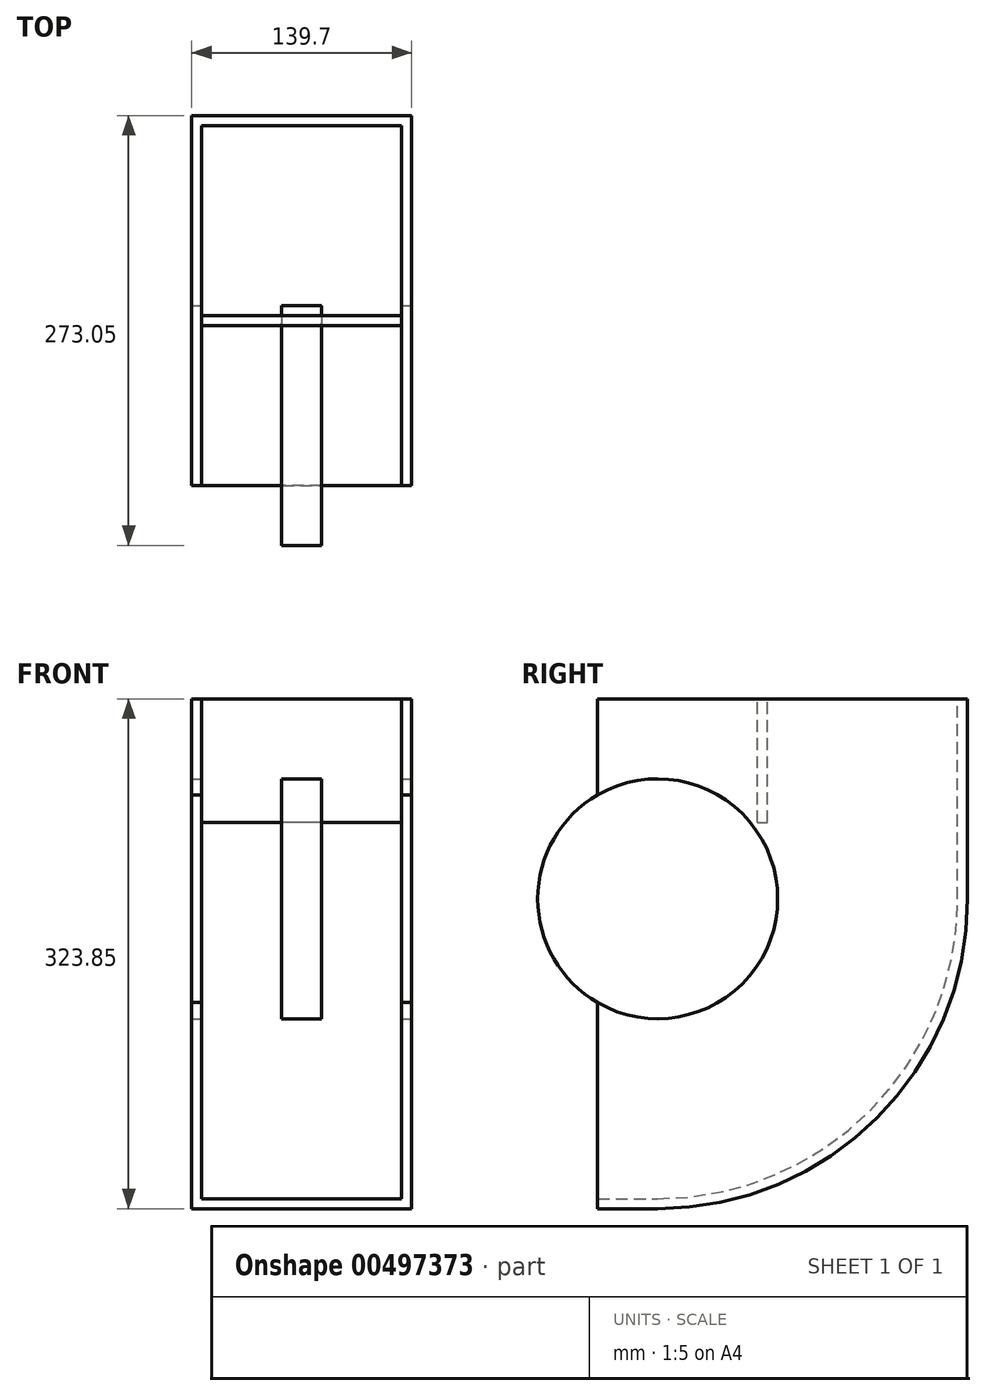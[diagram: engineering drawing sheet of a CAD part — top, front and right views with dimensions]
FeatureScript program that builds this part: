
annotation { "Feature Type Name" : "Feature", "Feature Type Description" : "" }
export const myFeature = defineFeature(function(context is Context, id is Id, definition is map)
    precondition{}
    {
        {
            var Q0;
            Q0=qCreatedBy(makeId("Right.planeOp"),FACE);
            var sketch = newSketch(context, id + "F0", { "sketchPlane" : qUnion([Q0])});
            skCircle(sketch, "E0", {"center": v(0, 0) * mm, "radius": 76.2 * mm});
            skLineSegment(sketch, "E1", {"start": v(0, 0) * mm, "end": v(0, -110.81) * mm});
            skLineSegment(sketch, "E2", {"start": v(0, -76.2) * mm, "end": v(0, -190.5) * mm});
            skCircle(sketch, "E3", {"center": v(0, 0) * mm, "radius": 190.5 * mm});
            skCircle(sketch, "E4.0", {"center": v(0, 0) * mm, "radius": 196.85 * mm});
            skLineSegment(sketch, "E5", {"start": v(0, -190.5) * mm, "end": v(-76.2, -190.5) * mm});
            skLineSegment(sketch, "E6", {"start": v(0, -196.85) * mm, "end": v(-76.2, -196.85) * mm});
            skLineSegment(sketch, "E7", {"start": v(-76.2, -196.85) * mm, "end": v(-76.2, -190.5) * mm});
            skLineSegment(sketch, "E8", {"start": v(0, 0) * mm, "end": v(403.67, 0) * mm});
            skLineSegment(sketch, "E9", {"start": v(196.85, 0) * mm, "end": v(196.85, 127) * mm});
            skLineSegment(sketch, "E10", {"start": v(190.5, 0) * mm, "end": v(190.5, 127) * mm});
            skLineSegment(sketch, "E11", {"start": v(190.5, 127) * mm, "end": v(196.85, 127) * mm});
            skLineSegment(sketch, "E12", {"start": v(0, -190.5) * mm, "end": v(0, -196.85) * mm});
            skSolve(sketch);
        }
        {
            var Q0;
            {var subQ0=sQuery(id+"F0.wireOp",EDGE,"E12");Q0=makeQuery(id+"F0.imprint","IMPRINT",FACE,{"disambiguationData":[TD([[makeQuery(id+"F0.imprint","IMPRINT",EDGE,{"derivedFrom":subQ0}),1.0]])]});}
            var Q1;
            {var subQ0=sQuery(id+"F0.wireOp",EDGE,"E9");Q1=makeQuery(id+"F0.imprint","IMPRINT",FACE,{"disambiguationData":[TD([[makeQuery(id+"F0.imprint","IMPRINT",EDGE,{"derivedFrom":subQ0}),1.0]])]});}
            var Q2;
            {var subQ1=sQuery(id+"F0.wireOp",EDGE,"E4.0");var subQ3=sQuery(id+"F0.wireOp",EDGE,"E10");var subQ4=makeQuery(id+"F0.imprint","INTERSECT",VERTEX,{"derivedFrom":[subQ1,subQ3]});Q2=makeQuery(id+"F0.imprint","IMPRINT",FACE,{"disambiguationData":[TD([[makeQuery(id+"F0.imprint","IMPRINT",EDGE,{"disambiguationData":[TD([[subQ4,1.0]])],"derivedFrom":subQ1}),1.0]])]});}
            extrude(context, id + "F1", {"entities" : qUnion([Q0, Q1, Q2]), "depth" : 63.5 * mm, "hasSecondDirection" : true, "secondDirectionOppositeDirection" : true, "secondDirectionDepth" : 63.5 * mm});
        }
        {
            var Q0;
            {var subQ0=sQuery(id+"F0.wireOp",EDGE,"E1");Q0=makeQuery(id+"F0.imprint","IMPRINT",FACE,{"disambiguationData":[TD([[makeQuery(id+"F0.imprint","IMPRINT",EDGE,{"derivedFrom":subQ0}),-1.0]])]});}
            var Q1;
            {var subQ0=sQuery(id+"F0.wireOp",EDGE,"E1");Q1=makeQuery(id+"F0.imprint","IMPRINT",FACE,{"disambiguationData":[TD([[makeQuery(id+"F0.imprint","IMPRINT",EDGE,{"derivedFrom":subQ0}),1.0]])]});}
            extrude(context, id + "F2", {"entities" : qUnion([Q0, Q1]), "depth" : 12.7 * mm, "hasSecondDirection" : true, "secondDirectionOppositeDirection" : true, "secondDirectionDepth" : 12.7 * mm});
        }
        {
            var Q0;
            Q0=makeQuery(id+"F1.opExtrude","CAP_FACE",FACE,{"disambiguationData":[OSD([sQuery(id+"F0.wireOp",EDGE,"E3"),sQuery(id+"F0.wireOp",EDGE,"E4.0"),sQuery(id+"F0.wireOp",EDGE,"E5"),sQuery(id+"F0.wireOp",EDGE,"E6"),sQuery(id+"F0.wireOp",EDGE,"E7"),sQuery(id+"F0.wireOp",EDGE,"E9"),sQuery(id+"F0.wireOp",EDGE,"E10"),sQuery(id+"F0.wireOp",EDGE,"E11")])],"isStart":true});
            var sketch = newSketch(context, id + "F3", { "sketchPlane" : qUnion([Q0])});
            skLineSegment(sketch, "E13.0", {"start": v(-196.85, 0) * mm, "end": v(-196.85, 127) * mm});
            skLineSegment(sketch, "E14.0", {"start": v(0, -196.85) * mm, "end": v(76.2, -196.85) * mm});
            skLineSegment(sketch, "E15.bottom", {"start": v(-196.85, 127) * mm, "end": v(76.2, 127) * mm});
            skLineSegment(sketch, "E15.top", {"start": v(-196.85, -196.85) * mm, "end": v(76.2, -196.85) * mm});
            skLineSegment(sketch, "E15.left", {"start": v(-196.85, 127) * mm, "end": v(-196.85, -196.85) * mm});
            skLineSegment(sketch, "E15.right", {"start": v(76.2, 127) * mm, "end": v(76.2, -196.85) * mm});
            skCircle(sketch, "E16.0", {"center": v(0, 0) * mm, "radius": 76.2 * mm});
            skLineSegment(sketch, "E17", {"start": v(0, 0) * mm, "end": v(38.1, 0) * mm});
            skLineSegment(sketch, "E18", {"start": v(38.1, 0) * mm, "end": v(38.1, 127) * mm});
            skLineSegment(sketch, "E19", {"start": v(38.1, 127) * mm, "end": v(38.1, -196.85) * mm});
            skSolve(sketch);
        }
        {
            var Q0;
            {var subQ0=sQuery(id+"F3.wireOp",EDGE,"E19");var subQ4=makeQuery(id+"F3.imprint","IMPRINT",VERTEX,{"derivedFrom":subQ0});Q0=makeQuery(id+"F3.imprint","IMPRINT",FACE,{"disambiguationData":[TD([[makeQuery(id+"F3.imprint","IMPRINT",EDGE,{"disambiguationData":[TD([[subQ4,1.0]])],"derivedFrom":subQ0}),-1.0]])]});}
            var Q1;
            {var subQ9=makeQuery(id+"F1.opExtrude","CAP_EDGE",EDGE,{"disambiguationData":[OSD([sQuery(id+"F0.wireOp",EDGE,"E3")])],"isStart":true});Q1=makeQuery(id+"F3.imprint","IMPRINT",FACE,{"disambiguationData":[TD([[makeQuery(id+"F3.imprint","IMPRINT",EDGE,{"derivedFrom":subQ9}),-1.0]])]});}
            var Q2;
            Q2=makeQuery(id+"F3.imprint","IMPRINT",FACE,{"disambiguationData":[TD([[makeQuery(id+"F3.imprint","IMPRINT",EDGE,{"derivedFrom":makeQuery(id+"F1.opExtrude","CAP_EDGE",EDGE,{"disambiguationData":[OSD([sQuery(id+"F0.wireOp",EDGE,"E3")])],"isStart":true})}),1.0]])]});
            extrude(context, id + "F4", {"entities" : qUnion([Q0, Q1, Q2]), "depth" : 6.35 * mm});
        }
        {
            var Q0;
            Q0=makeQuery(id+"F4.opExtrude","CAP_FACE",FACE,{"disambiguationData":[OSD([sQuery(id+"F3.wireOp",EDGE,"E15.bottom"),sQuery(id+"F3.wireOp",EDGE,"E15.top"),sQuery(id+"F3.wireOp",EDGE,"E15.left"),sQuery(id+"F3.wireOp",EDGE,"E15.right")])],"isStart":false});
            var sketch = newSketch(context, id + "F5", { "sketchPlane" : qUnion([Q0])});
            skCircle(sketch, "E20.0", {"center": v(0, 0) * mm, "radius": 76.2 * mm});
            skCircle(sketch, "E21", {"center": v(0, 0) * mm, "radius": 9.53 * mm});
            skCircle(sketch, "E22", {"center": v(0, 25.4) * mm, "radius": 4.45 * mm});
            skCircle(sketch, "E23", {"center": v(0, -25.4) * mm, "radius": 4.45 * mm});
            skSolve(sketch);
        }
        {
            var Q0;
            Q0=makeQuery(id+"F5.imprint","IMPRINT",FACE,{"disambiguationData":[TD([[makeQuery(id+"F5.imprint","IMPRINT",EDGE,{"derivedFrom":sQuery(id+"F5.wireOp",EDGE,"E22")}),1.0]])]});
            var Q1;
            Q1=makeQuery(id+"F5.imprint","IMPRINT",FACE,{"disambiguationData":[TD([[makeQuery(id+"F5.imprint","IMPRINT",EDGE,{"derivedFrom":sQuery(id+"F5.wireOp",EDGE,"E21")}),1.0]])]});
            var Q2;
            Q2=makeQuery(id+"F5.imprint","IMPRINT",FACE,{"disambiguationData":[TD([[makeQuery(id+"F5.imprint","IMPRINT",EDGE,{"derivedFrom":sQuery(id+"F5.wireOp",EDGE,"E23")}),1.0]])]});
            extrude(context, id + "F6", {"entities" : qUnion([Q0, Q1, Q2]), "operationType" : NewBodyOperationType.REMOVE, "oppositeDirection" : true, "depth" : 25.4 * mm});
        }
        {
            var Q0;
            Q0=makeQuery(id+"F1.opExtrude","SWEPT_FACE",FACE,{"disambiguationData":[OSD([sQuery(id+"F0.wireOp",EDGE,"E9")])]});
            var sketch = newSketch(context, id + "F7", { "sketchPlane" : qUnion([Q0])});
            skLineSegment(sketch, "E24.0", {"start": v(69.85, 127) * mm, "end": v(63.5, 127) * mm});
            skLineSegment(sketch, "E25", {"start": v(69.85, 127) * mm, "end": v(-63.5, 127) * mm});
            skSolve(sketch);
        }
        {
            var Q0;
            Q0=makeQuery(id+"F4.opExtrude","SWEPT_BODY",BODY,{"disambiguationData":[OSD([sQuery(id+"F3.wireOp",EDGE,"E15.bottom"),sQuery(id+"F3.wireOp",EDGE,"E15.top"),sQuery(id+"F3.wireOp",EDGE,"E15.left"),sQuery(id+"F3.wireOp",EDGE,"E15.right")])]});
            var Q1;
            Q1=sQuery(id+"F7.wireOp",VERTEX,"E25.start");
            var Q2;
            Q2=sQuery(id+"F7.wireOp",VERTEX,"E25.end");
            transform(context, id + "F8", {"entities" : qUnion([Q0]), "transformType" : TransformType.TRANSLATION_ENTITY, "oppositeDirectionEntity" : false, "transformLine" : qUnion([Q1, Q2]), "makeCopy" : true});
        }
        {
            var Q0;
            Q0=makeQuery(id+"F4.opExtrude","CAP_FACE",FACE,{"disambiguationData":[OSD([sQuery(id+"F3.wireOp",EDGE,"E15.bottom"),sQuery(id+"F3.wireOp",EDGE,"E15.top"),sQuery(id+"F3.wireOp",EDGE,"E15.left"),sQuery(id+"F3.wireOp",EDGE,"E15.right")])],"isStart":true});
            var sketch = newSketch(context, id + "F9", { "sketchPlane" : qUnion([Q0])});
            skCircle(sketch, "E26.0", {"center": v(0, 0) * mm, "radius": 76.2 * mm});
            skCircle(sketch, "E27.0", {"center": v(0, 0) * mm, "radius": 69.85 * mm});
            skLineSegment(sketch, "E28", {"start": v(0, 2.21) * mm, "end": v(76.2, 0) * mm});
            skCircle(sketch, "E29.0", {"center": v(0, 0) * mm, "radius": 63.5 * mm});
            skLineSegment(sketch, "E30", {"start": v(69.85, 0.18) * mm, "end": v(69.85, 127) * mm});
            skLineSegment(sketch, "E31", {"start": v(63.5, 0.37) * mm, "end": v(63.5, 127) * mm});
            skPoint(sketch, "E31.endSnap0", {"position": v(79.37, 127) * mm});
            skLineSegment(sketch, "E32", {"start": v(63.5, 127) * mm, "end": v(69.85, 127) * mm});
            skLineSegment(sketch, "E33", {"start": v(63.5, 42.12) * mm, "end": v(69.85, 42.12) * mm});
            skLineSegment(sketch, "E34.0", {"start": v(63.5, 48.47) * mm, "end": v(69.85, 48.47) * mm});
            skSolve(sketch);
        }
        {
            var Q0;
            {var subQ0=sQuery(id+"F9.wireOp",EDGE,"E32");Q0=makeQuery(id+"F9.imprint","IMPRINT",FACE,{"disambiguationData":[TD([[makeQuery(id+"F9.imprint","IMPRINT",EDGE,{"derivedFrom":subQ0}),1.0]])]});}
            var Q1;
            Q1=makeQuery(id+"F1.opExtrude","CAP_FACE",FACE,{"disambiguationData":[OSD([sQuery(id+"F0.wireOp",EDGE,"E3"),sQuery(id+"F0.wireOp",EDGE,"E4.0"),sQuery(id+"F0.wireOp",EDGE,"E5"),sQuery(id+"F0.wireOp",EDGE,"E6"),sQuery(id+"F0.wireOp",EDGE,"E7"),sQuery(id+"F0.wireOp",EDGE,"E9"),sQuery(id+"F0.wireOp",EDGE,"E10"),sQuery(id+"F0.wireOp",EDGE,"E11")])],"isStart":false});
            extrude(context, id + "F10", {"entities" : qUnion([Q0]), "endBound" : BoundingType.UP_TO_SURFACE, "endBoundEntityFace" : qUnion([Q1]), "depth" : 25.4 * mm});
        }
        {
            var Q0;
            Q0=makeQuery(id+"F1.opExtrude","SWEPT_FACE",FACE,{"disambiguationData":[OSD([sQuery(id+"F0.wireOp",EDGE,"E12")])]});
            var Q1;
            Q1=makeQuery(id+"F8.opPattern","COPY",FACE,{"derivedFrom":makeQuery(id+"F4.opExtrude","SWEPT_FACE",FACE,{"disambiguationData":[OSD([sQuery(id+"F3.wireOp",EDGE,"E19")])]}),"instanceName":"1"});
            extrude(context, id + "F11", {"entities" : qUnion([Q0]), "operationType" : NewBodyOperationType.ADD, "endBound" : BoundingType.UP_TO_SURFACE, "endBoundEntityFace" : qUnion([Q1]), "depth" : 25.4 * mm});
        }
    });
